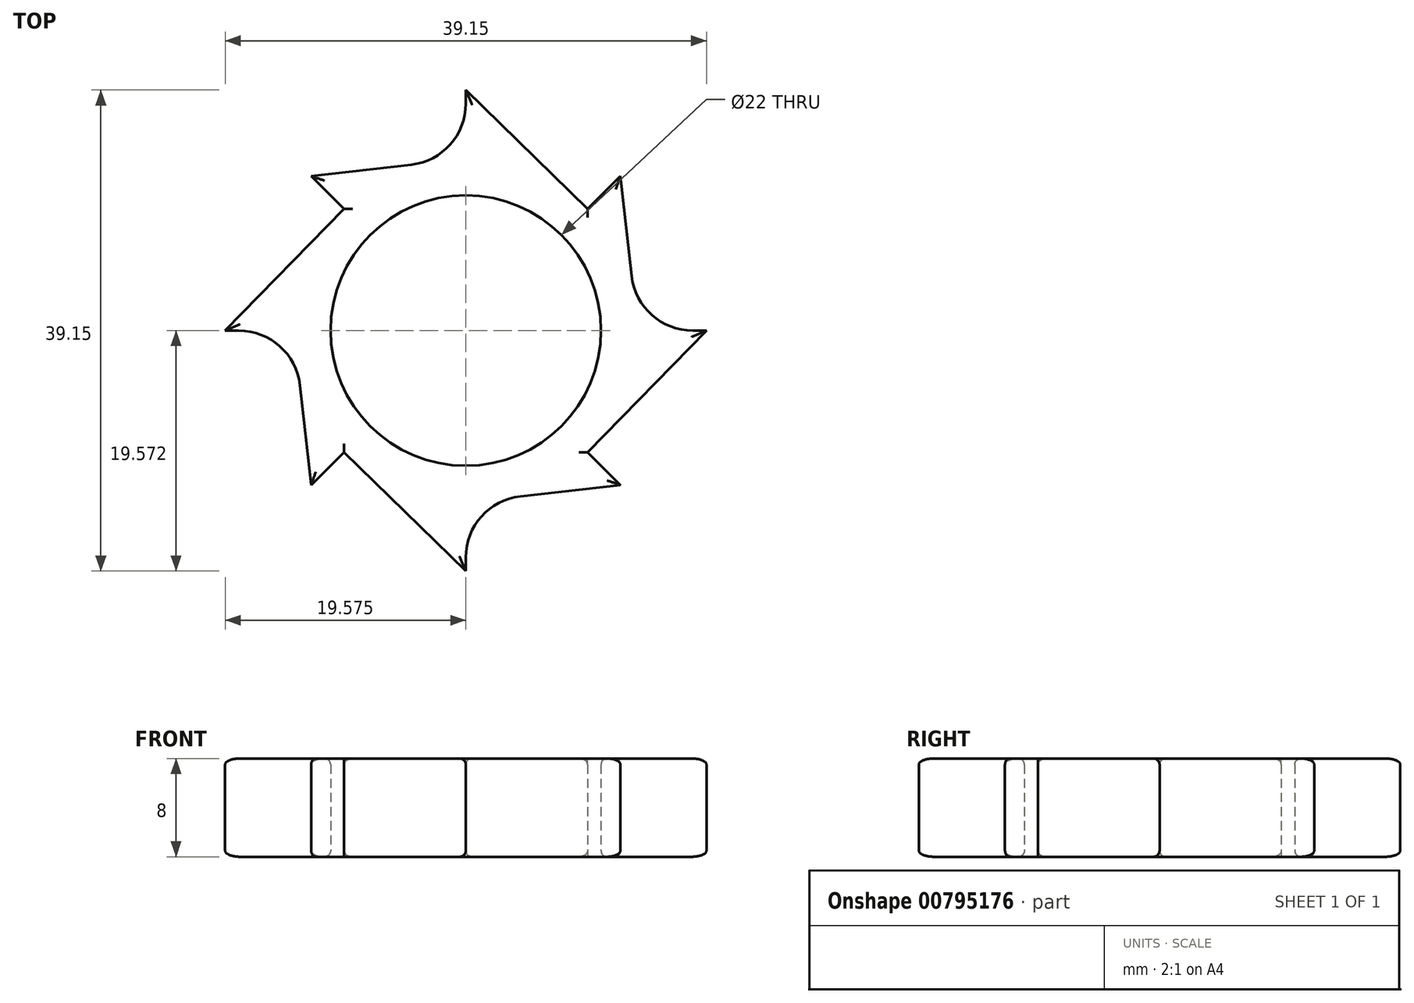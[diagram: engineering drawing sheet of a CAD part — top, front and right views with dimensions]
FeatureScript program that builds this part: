
annotation { "Feature Type Name" : "Feature", "Feature Type Description" : "" }
export const myFeature = defineFeature(function(context is Context, id is Id, definition is map)
    precondition{}
    {
        {
            var Q0;
            Q0=qCreatedBy(makeId("Top.planeOp"),FACE);
            var sketch = newSketch(context, id + "F0", { "sketchPlane" : qUnion([Q0])});
            skCircle(sketch, "E0", {"center": v(-75.28, 45.77) * mm, "radius": 11 * mm});
            skCircle(sketch, "E1.0", {"center": v(-75.28, 45.77) * mm, "radius": 14 * mm});
            skLineSegment(sketch, "E2", {"start": v(-87.85, 33.2) * mm, "end": v(-85.17, 35.87) * mm});
            skLineSegment(sketch, "E3", {"start": v(-62.7, 33.2) * mm, "end": v(-65.38, 35.87) * mm});
            skLineSegment(sketch, "E4", {"start": v(-62.7, 58.35) * mm, "end": v(-65.38, 55.67) * mm});
            skLineSegment(sketch, "E5", {"start": v(-87.85, 58.35) * mm, "end": v(-85.17, 55.67) * mm});
            skLineSegment(sketch, "E6", {"start": v(-87.85, 58.35) * mm, "end": v(-79.71, 59.27) * mm});
            skLineSegment(sketch, "E7", {"start": v(-94.85, 45.77) * mm, "end": v(-85.17, 55.67) * mm});
            skLineSegment(sketch, "E8", {"start": v(-87.85, 33.2) * mm, "end": v(-88.77, 41.33) * mm});
            skLineSegment(sketch, "E9", {"start": v(-75.28, 26.2) * mm, "end": v(-85.17, 35.87) * mm});
            skLineSegment(sketch, "E10", {"start": v(-62.7, 33.2) * mm, "end": v(-70.84, 32.27) * mm});
            skLineSegment(sketch, "E11", {"start": v(-55.7, 45.77) * mm, "end": v(-65.38, 35.87) * mm});
            skLineSegment(sketch, "E12", {"start": v(-62.7, 58.35) * mm, "end": v(-61.78, 50.2) * mm});
            skLineSegment(sketch, "E13", {"start": v(-75.28, 65.35) * mm, "end": v(-65.38, 55.67) * mm});
            skLineSegment(sketch, "E14", {"start": v(-75.28, 27.3) * mm, "end": v(-75.28, 26.2) * mm});
            skLineSegment(sketch, "E15", {"start": v(-94.85, 45.77) * mm, "end": v(-93.74, 45.77) * mm});
            skLineSegment(sketch, "E16", {"start": v(-75.28, 65.35) * mm, "end": v(-75.28, 64.24) * mm});
            skLineSegment(sketch, "E17", {"start": v(-55.7, 45.77) * mm, "end": v(-56.81, 45.77) * mm});
            skPoint(sketch, "E18.visualSharp", {"position": v(-75.28, 59.77) * mm});
            skArc(sketch, "E18.filletArc", {"start": v(-79.71, 59.27) * mm, "mid": v(-76.55, 60.9) * mm, "end": v(-75.28, 64.24) * mm});
            skPoint(sketch, "E19.visualSharp", {"position": v(-61.28, 45.77) * mm});
            skArc(sketch, "E19.filletArc", {"start": v(-61.78, 50.2) * mm, "mid": v(-60.14, 47.04) * mm, "end": v(-56.81, 45.77) * mm});
            skPoint(sketch, "E20.visualSharp", {"position": v(-75.28, 31.77) * mm});
            skArc(sketch, "E20.filletArc", {"start": v(-70.84, 32.27) * mm, "mid": v(-74, 30.64) * mm, "end": v(-75.28, 27.3) * mm});
            skPoint(sketch, "E21.visualSharp", {"position": v(-89.28, 45.77) * mm});
            skArc(sketch, "E21.filletArc", {"start": v(-88.77, 41.33) * mm, "mid": v(-90.41, 44.5) * mm, "end": v(-93.74, 45.77) * mm});
            skSolve(sketch);
        }
        {
            var Q0;
            {var subQ4=sQuery(id+"F0.wireOp",EDGE,"E5");Q0=makeQuery(id+"F0.imprint","IMPRINT",FACE,{"disambiguationData":[TD([[makeQuery(id+"F0.imprint","IMPRINT",EDGE,{"derivedFrom":subQ4}),1.0]])]});}
            var Q1;
            {var subQ0=sQuery(id+"F0.wireOp",EDGE,"E4");Q1=makeQuery(id+"F0.imprint","IMPRINT",FACE,{"disambiguationData":[TD([[makeQuery(id+"F0.imprint","IMPRINT",EDGE,{"derivedFrom":subQ0}),1.0]])]});}
            var Q2;
            {var subQ4=sQuery(id+"F0.wireOp",EDGE,"E3");Q2=makeQuery(id+"F0.imprint","IMPRINT",FACE,{"disambiguationData":[TD([[makeQuery(id+"F0.imprint","IMPRINT",EDGE,{"derivedFrom":subQ4}),1.0]])]});}
            var Q3;
            {var subQ4=sQuery(id+"F0.wireOp",EDGE,"E2");Q3=makeQuery(id+"F0.imprint","IMPRINT",FACE,{"disambiguationData":[TD([[makeQuery(id+"F0.imprint","IMPRINT",EDGE,{"derivedFrom":subQ4}),1.0]])]});}
            var Q4;
            Q4=makeQuery(id+"F0.imprint","IMPRINT",FACE,{"disambiguationData":[TD([[makeQuery(id+"F0.imprint","IMPRINT",EDGE,{"derivedFrom":sQuery(id+"F0.wireOp",EDGE,"E0")}),-1.0]])]});
            extrude(context, id + "F1", {"entities" : qUnion([Q0, Q1, Q2, Q3, Q4]), "depth" : 8 * mm, "offsetDistance" : 25 * mm});
        }
        {
            var Q0;
            Q0=makeQuery(id+"F1.opExtrude","CAP_FACE",FACE,{"disambiguationData":[OSD([sQuery(id+"F0.wireOp",EDGE,"E0"),sQuery(id+"F0.wireOp",EDGE,"E2"),sQuery(id+"F0.wireOp",EDGE,"E3"),sQuery(id+"F0.wireOp",EDGE,"E4"),sQuery(id+"F0.wireOp",EDGE,"E5"),sQuery(id+"F0.wireOp",EDGE,"E6"),sQuery(id+"F0.wireOp",EDGE,"E7"),sQuery(id+"F0.wireOp",EDGE,"E8"),sQuery(id+"F0.wireOp",EDGE,"E9"),sQuery(id+"F0.wireOp",EDGE,"E10"),sQuery(id+"F0.wireOp",EDGE,"E11"),sQuery(id+"F0.wireOp",EDGE,"E12"),sQuery(id+"F0.wireOp",EDGE,"E13"),sQuery(id+"F0.wireOp",EDGE,"E14"),sQuery(id+"F0.wireOp",EDGE,"E15"),sQuery(id+"F0.wireOp",EDGE,"E16"),sQuery(id+"F0.wireOp",EDGE,"E17"),sQuery(id+"F0.wireOp",EDGE,"E18.filletArc"),sQuery(id+"F0.wireOp",EDGE,"E19.filletArc"),sQuery(id+"F0.wireOp",EDGE,"E20.filletArc"),sQuery(id+"F0.wireOp",EDGE,"E21.filletArc")])],"isStart":false});
            var Q1;
            Q1=makeQuery(id+"F1.opExtrude","CAP_FACE",FACE,{"disambiguationData":[OSD([sQuery(id+"F0.wireOp",EDGE,"E0"),sQuery(id+"F0.wireOp",EDGE,"E2"),sQuery(id+"F0.wireOp",EDGE,"E3"),sQuery(id+"F0.wireOp",EDGE,"E4"),sQuery(id+"F0.wireOp",EDGE,"E5"),sQuery(id+"F0.wireOp",EDGE,"E6"),sQuery(id+"F0.wireOp",EDGE,"E7"),sQuery(id+"F0.wireOp",EDGE,"E8"),sQuery(id+"F0.wireOp",EDGE,"E9"),sQuery(id+"F0.wireOp",EDGE,"E10"),sQuery(id+"F0.wireOp",EDGE,"E11"),sQuery(id+"F0.wireOp",EDGE,"E12"),sQuery(id+"F0.wireOp",EDGE,"E13"),sQuery(id+"F0.wireOp",EDGE,"E14"),sQuery(id+"F0.wireOp",EDGE,"E15"),sQuery(id+"F0.wireOp",EDGE,"E16"),sQuery(id+"F0.wireOp",EDGE,"E17"),sQuery(id+"F0.wireOp",EDGE,"E18.filletArc"),sQuery(id+"F0.wireOp",EDGE,"E19.filletArc"),sQuery(id+"F0.wireOp",EDGE,"E20.filletArc"),sQuery(id+"F0.wireOp",EDGE,"E21.filletArc")])],"isStart":true});
            fillet(context, id + "F2", {"entities" : qUnion([Q0, Q1]), "radius" : .5 * mm, "tangentPropagation" : true, "allowEdgeOverflow" : false});
        }
    });
